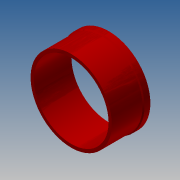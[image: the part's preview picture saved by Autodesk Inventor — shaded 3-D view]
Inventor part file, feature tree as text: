
AUTODESK INVENTOR PART (.ipt)
format: ipt  version: 2017.3 (Build 213257000, 257)  size: 121,344 bytes
history: native  units: in
note: dims shown in document units (in); Inventor stores cm internally (conversion verified against a paired STEP export)
features: other x3, extrude x2, sketch x2, chamfer x1
ambient origin geometry x8: Origin, YZ Plane, XZ Plane, XY Plane, X Axis, Y Axis, Z Axis, Center Point
bodies: Solid1 (feature_tree)
feature tree (8):
  other  "A1-19027-400-08 HCWI liner - pup.ipt"
  extrude  "Extrusion1"  Depth=0.5in TaperAngle=0.0deg
  extrude  "Extrusion2"  Depth=0.5in
  chamfer  "Chamfer1"  Distance=0.25in Angle=45.0deg
  other  "Solid1::A1-19027-400-08 HCWI liner - pup.ipt"
  other  "TaggingFeature1"
  sketch  "Sketch2"  dims[d0=0.3937in d1=0.5in d2=2.0in d3=0.0in d4=0.0in]
  sketch  "Sketch3"  dims[d5=0.5in d6=0.5in d7=0.0in d8=0.0in d9=0.25in d10=0.25in d11=0.125in d12=45.0deg]
